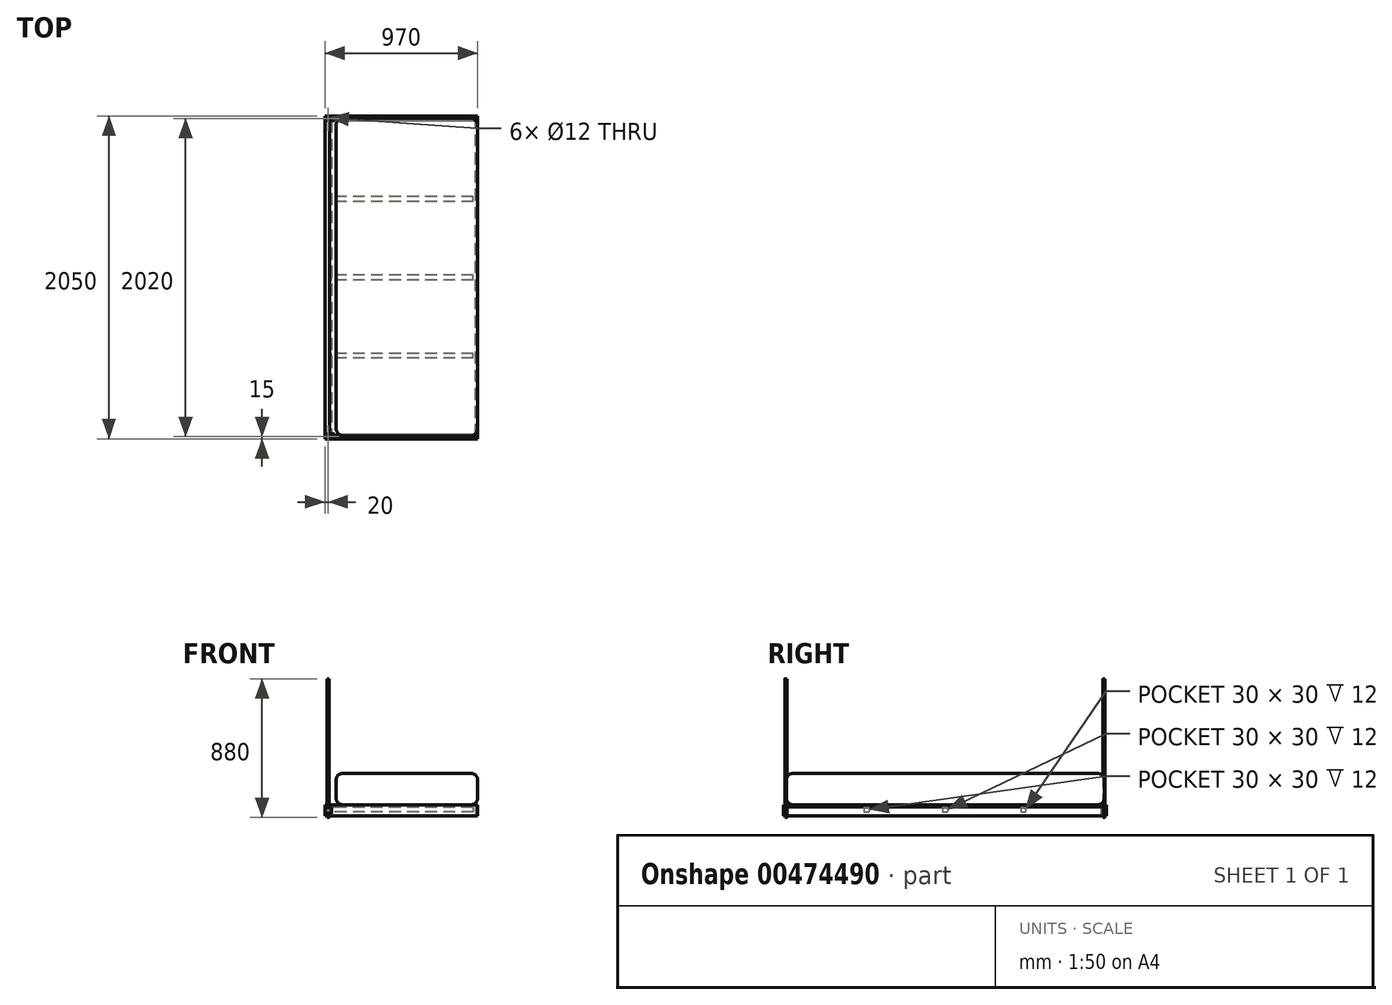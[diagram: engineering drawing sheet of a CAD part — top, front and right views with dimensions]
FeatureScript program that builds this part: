
annotation { "Feature Type Name" : "Feature", "Feature Type Description" : "" }
export const myFeature = defineFeature(function(context is Context, id is Id, definition is map)
    precondition{}
    {
        {
            var Q0;
            Q0=qCreatedBy(makeId("Top.planeOp"),FACE);
            var sketch = newSketch(context, id + "F0", { "sketchPlane" : qUnion([Q0])});
            skLineSegment(sketch, "E0.bottom", {"start": v(0, 0) * mm, "end": v(970, 0) * mm});
            skLineSegment(sketch, "E0.top", {"start": v(0, 2050) * mm, "end": v(970, 2050) * mm});
            skLineSegment(sketch, "E0.left", {"start": v(0, 0) * mm, "end": v(0, 2050) * mm});
            skLineSegment(sketch, "E0.right", {"start": v(970, 0) * mm, "end": v(970, 2050) * mm});
            skSolve(sketch);
        }
        {
            var Q0;
            Q0=qCreatedBy(makeId("Front.planeOp"),FACE);
            var sketch = newSketch(context, id + "F1", { "sketchPlane" : qUnion([Q0])});
            skLineSegment(sketch, "E1.bottom", {"start": v(0, 0) * mm, "end": v(42, 0) * mm});
            skLineSegment(sketch, "E1.top", {"start": v(0, 70) * mm, "end": v(30, 70) * mm});
            skLineSegment(sketch, "E1.left", {"start": v(0, 0) * mm, "end": v(0, 70) * mm});
            skLineSegment(sketch, "E1.right", {"start": v(30, 58.33) * mm, "end": v(30, 70) * mm});
            skLineSegment(sketch, "E2.bottom", {"start": v(30, 58.33) * mm, "end": v(42, 58.33) * mm});
            skLineSegment(sketch, "E2.right", {"start": v(42, 58.33) * mm, "end": v(42, 0) * mm});
            skSolve(sketch);
        }
        {
            var Q0;
            Q0 = qSketchRegion(id + "F1", true);
            var Q1;
            Q1=sQuery(id+"F0.wireOp",VERTEX,"E0.left.end");
            extrude(context, id + "F2", {"entities" : qUnion([Q0]), "endBound" : BoundingType.UP_TO_VERTEX, "oppositeDirection" : true, "endBoundEntityVertex" : qUnion([Q1]), "depth" : 25 * mm});
        }
        {
            var Q0;
            Q0=makeQuery(id+"F2.opExtrude","SWEPT_FACE",FACE,{"disambiguationData":[OSD([sQuery(id+"F1.wireOp",EDGE,"E1.left")])]});
            var sketch = newSketch(context, id + "F3", { "sketchPlane" : qUnion([Q0])});
            skLineSegment(sketch, "E3.bottom", {"start": v(0, 70) * mm, "end": v(-30, 70) * mm});
            skLineSegment(sketch, "E3.top", {"start": v(0, 55) * mm, "end": v(-30, 55) * mm});
            skLineSegment(sketch, "E3.left", {"start": v(0, 70) * mm, "end": v(0, 55) * mm});
            skLineSegment(sketch, "E3.right", {"start": v(-30, 70) * mm, "end": v(-30, 55) * mm});
            skLineSegment(sketch, "E4.bottom", {"start": v(0, 15) * mm, "end": v(-30, 15) * mm});
            skLineSegment(sketch, "E4.top", {"start": v(0, 0) * mm, "end": v(-30, 0) * mm});
            skLineSegment(sketch, "E4.left", {"start": v(0, 15) * mm, "end": v(0, 0) * mm});
            skLineSegment(sketch, "E4.right", {"start": v(-30, 15) * mm, "end": v(-30, 0) * mm});
            skLineSegment(sketch, "E5", {"start": v(-1025, 70) * mm, "end": v(-1025, 0) * mm, "construction": true});
            skLineSegment(sketch, "E6.MirrorCS", {"start": v(-2020, 70) * mm, "end": v(-2020, 55) * mm});
            skLineSegment(sketch, "E7.MirrorCS", {"start": v(-2050, 15) * mm, "end": v(-2020, 15) * mm});
            skLineSegment(sketch, "E8.MirrorCS", {"start": v(-2050, 0) * mm, "end": v(-2020, 0) * mm});
            skLineSegment(sketch, "E9.MirrorCS", {"start": v(-2020, 15) * mm, "end": v(-2020, 0) * mm});
            skLineSegment(sketch, "E10.MirrorCS", {"start": v(-2050, 55) * mm, "end": v(-2020, 55) * mm});
            skLineSegment(sketch, "E11.MirrorCS", {"start": v(-2050, 15) * mm, "end": v(-2050, 0) * mm});
            skLineSegment(sketch, "E12.MirrorCS", {"start": v(-2050, 70) * mm, "end": v(-2020, 70) * mm});
            skLineSegment(sketch, "E13.MirrorCS", {"start": v(-2050, 70) * mm, "end": v(-2050, 55) * mm});
            skSolve(sketch);
        }
        {
            var Q0;
            Q0 = qSketchRegion(id + "F3", true);
            extrude(context, id + "F4", {"entities" : qUnion([Q0]), "operationType" : NewBodyOperationType.REMOVE, "endBound" : BoundingType.THROUGH_ALL, "oppositeDirection" : true, "depth" : 25 * mm});
        }
        {
            var Q0;
            Q0=makeQuery(id+"F2.opExtrude","SWEPT_FACE",FACE,{"disambiguationData":[OSD([sQuery(id+"F1.wireOp",EDGE,"E2.right")])]});
            var sketch = newSketch(context, id + "F5", { "sketchPlane" : qUnion([Q0])});
            skLineSegment(sketch, "E14.bottom", {"start": v(512.5, 55) * mm, "end": v(542.5, 55) * mm});
            skLineSegment(sketch, "E14.top", {"start": v(512.5, 25) * mm, "end": v(542.5, 25) * mm});
            skLineSegment(sketch, "E14.left", {"start": v(512.5, 55) * mm, "end": v(512.5, 25) * mm});
            skLineSegment(sketch, "E14.right", {"start": v(542.5, 55) * mm, "end": v(542.5, 25) * mm});
            skLineSegment(sketch, "E15.1.0.0", {"start": v(1040, 55) * mm, "end": v(1040, 25) * mm});
            skLineSegment(sketch, "E15.1.0.1", {"start": v(1010, 55) * mm, "end": v(1010, 25) * mm});
            skLineSegment(sketch, "E15.1.0.2", {"start": v(1010, 25) * mm, "end": v(1040, 25) * mm});
            skLineSegment(sketch, "E15.1.0.3", {"start": v(1010, 55) * mm, "end": v(1040, 55) * mm});
            skLineSegment(sketch, "E15.2.0.0", {"start": v(1537.5, 55) * mm, "end": v(1537.5, 25) * mm});
            skLineSegment(sketch, "E15.2.0.1", {"start": v(1507.5, 55) * mm, "end": v(1507.5, 25) * mm});
            skLineSegment(sketch, "E15.2.0.2", {"start": v(1507.5, 25) * mm, "end": v(1537.5, 25) * mm});
            skLineSegment(sketch, "E15.2.0.3", {"start": v(1507.5, 55) * mm, "end": v(1537.5, 55) * mm});
            skLineSegment(sketch, "E15.direction1", {"start": v(512.5, 25) * mm, "end": v(1010, 25) * mm, "construction": true});
            skLineSegment(sketch, "E16", {"start": v(1025, 25) * mm, "end": v(1025, 0) * mm, "construction": true});
            skSolve(sketch);
        }
        {
            var Q0;
            Q0 = qSketchRegion(id + "F5", true);
            var Q1;
            Q1=makeQuery(id+"F2.opExtrude","SWEPT_FACE",FACE,{"disambiguationData":[OSD([sQuery(id+"F1.wireOp",EDGE,"E1.right")])]});
            extrude(context, id + "F6", {"entities" : qUnion([Q0]), "operationType" : NewBodyOperationType.REMOVE, "endBound" : BoundingType.UP_TO_SURFACE, "oppositeDirection" : true, "endBoundEntityFace" : qUnion([Q1]), "depth" : 25 * mm});
        }
        {
            var Q0;
            Q0 = qSketchRegion(id + "F5", true);
            var Q1;
            {var subQ0=sQuery(id+"F1.wireOp",EDGE,"E1.right");Q1=makeQuery(id+"F6.boolean.opBoolean","MERGE",FACE,{"derivedFrom":[makeQuery(id+"F2.opExtrude","SWEPT_FACE",FACE,{"disambiguationData":[OSD([subQ0])]}),makeQuery(id+"F6.opExtrude","CAP_FACE",FACE,{"disambiguationData":[OSD([subQ0]),ownerDisambiguation([makeQuery(id+"F5.imprint","IMPRINT",EDGE,{"derivedFrom":sQuery(id+"F5.wireOp",EDGE,"E14.bottom")})])],"isStart":false}),makeQuery(id+"F6.opExtrude","CAP_FACE",FACE,{"disambiguationData":[OSD([subQ0]),ownerDisambiguation([makeQuery(id+"F5.imprint","IMPRINT",EDGE,{"derivedFrom":sQuery(id+"F5.wireOp",EDGE,"E15.1.0.0")})])],"isStart":false}),makeQuery(id+"F6.opExtrude","CAP_FACE",FACE,{"disambiguationData":[OSD([subQ0]),ownerDisambiguation([makeQuery(id+"F5.imprint","IMPRINT",EDGE,{"derivedFrom":sQuery(id+"F5.wireOp",EDGE,"E15.2.0.0")})])],"isStart":false}),makeQuery(id+"F6.opExtrude","CAP_FACE",FACE,{"disambiguationData":[OSD([subQ0]),ownerDisambiguation([makeQuery(id+"F5.imprint","IMPRINT",EDGE,{"derivedFrom":sQuery(id+"F5.wireOp",EDGE,"E15.3.0.0")})])],"isStart":false})]});}
            extrude(context, id + "F7", {"entities" : qUnion([Q0]), "depth" : 900 * mm, "hasSecondDirection" : true, "secondDirectionBound" : SecondDirectionBoundingType.UP_TO_SURFACE, "secondDirectionOppositeDirection" : true, "secondDirectionBoundEntityFace" : qUnion([Q1]), "secondDirectionDepth" : 25 * mm});
        }
        {
            var Q0;
            {var subQ0=sQuery(id+"F1.wireOp",EDGE,"E1.bottom");var subQ1=sQuery(id+"F1.wireOp",EDGE,"E1.left");var subQ2=sQuery(id+"F1.wireOp",EDGE,"E2.right");Q0=makeQuery(id+"F4.boolean.opBoolean","SPLIT",FACE,{"disambiguationData":[TD([makeQuery(id+"F2.opExtrude","SWEPT_FACE",FACE,{"disambiguationData":[OSD([subQ0])]})])],"derivedFrom":makeQuery(id+"F2.opExtrude","CAP_FACE",FACE,{"disambiguationData":[OSD([subQ0,sQuery(id+"F1.wireOp",EDGE,"E1.top"),subQ1,sQuery(id+"F1.wireOp",EDGE,"E1.right"),sQuery(id+"F1.wireOp",EDGE,"E2.bottom"),subQ2])],"isStart":true})});}
            var sketch = newSketch(context, id + "F8", { "sketchPlane" : qUnion([Q0])});
            skLineSegment(sketch, "E17.0.0", {"start": v(42, 15) * mm, "end": v(0, 15) * mm});
            skLineSegment(sketch, "E18.1", {"start": v(0, 70) * mm, "end": v(0, 55) * mm});
            skLineSegment(sketch, "E19", {"start": v(0, 70) * mm, "end": v(970, 70) * mm});
            skLineSegment(sketch, "E20", {"start": v(970, 70) * mm, "end": v(970, 0) * mm});
            skLineSegment(sketch, "E21.1", {"start": v(42, 55) * mm, "end": v(42, 55) * mm});
            skPoint(sketch, "E21.3", {"position": v(42, 35) * mm});
            skLineSegment(sketch, "E22.0", {"start": v(42, 55) * mm, "end": v(42, 15) * mm});
            skLineSegment(sketch, "E22.1", {"start": v(42, 55) * mm, "end": v(0, 55) * mm});
            skLineSegment(sketch, "E23", {"start": v(42, 0) * mm, "end": v(970, 0) * mm});
            skLineSegment(sketch, "E24", {"start": v(0, 15) * mm, "end": v(0, 0) * mm});
            skLineSegment(sketch, "E25", {"start": v(0, 0) * mm, "end": v(42, 0) * mm});
            skSolve(sketch);
        }
        {
            var Q0;
            Q0 = qSketchRegion(id + "F8", true);
            var Q1;
            Q1=makeQuery(id+"F4.boolean.opBoolean","COPY",FACE,{"derivedFrom":makeQuery(id+"F4.opExtrude","SWEPT_FACE",FACE,{"disambiguationData":[OSD([sQuery(id+"F3.wireOp",EDGE,"E4.right")])]})});
            extrude(context, id + "F9", {"entities" : qUnion([Q0]), "endBound" : BoundingType.UP_TO_SURFACE, "oppositeDirection" : true, "endBoundEntityFace" : qUnion([Q1]), "depth" : 25 * mm});
        }
        {
            var Q0;
            Q0=sQuery(id+"F0.wireOp",EDGE,"E0.left");
            cPoint(context, id + "F10", {"entities" : qUnion([Q0]), "parameter" : 0.5});
        }
        {
            var Q0;
            Q0=qCreatedBy(makeId("Front.planeOp"),FACE);
            var Q1;
            Q1 = qCreatedBy(id + "F10" ,VERTEX);
            cPlane(context, id + "F11", {"entities" : qUnion([Q0, Q1]), "cplaneType" : CPlaneType.PLANE_POINT, "offset" : 25 * mm, "width" : 150 * mm, "height" : 150 * mm});
        }
        {
            var Q0;
            Q0=makeQuery(id+"F9.opExtrude","SWEPT_FACE",FACE,{"disambiguationData":[OSD([sQuery(id+"F8.wireOp",EDGE,"E19")])]});
            var sketch = newSketch(context, id + "F12", { "sketchPlane" : qUnion([Q0])});
            skLineSegment(sketch, "E26.bottom", {"start": v(60, 30) * mm, "end": v(970, 30) * mm});
            skLineSegment(sketch, "E26.top", {"start": v(60, 18) * mm, "end": v(970, 18) * mm});
            skLineSegment(sketch, "E26.left", {"start": v(60, 30) * mm, "end": v(60, 18) * mm});
            skLineSegment(sketch, "E26.right", {"start": v(970, 30) * mm, "end": v(970, 18) * mm});
            skSolve(sketch);
        }
        {
            var Q0;
            Q0 = qSketchRegion(id + "F12", true);
            var Q1;
            {var subQ3=sQuery(id+"F1.wireOp",EDGE,"E2.bottom");Q1=makeQuery(id+"F6.boolean.opBoolean","SPLIT",FACE,{"disambiguationData":[TD([makeQuery(id+"F4.boolean.opBoolean","COPY",FACE,{"derivedFrom":makeQuery(id+"F4.opExtrude","SWEPT_FACE",FACE,{"disambiguationData":[OSD([sQuery(id+"F3.wireOp",EDGE,"E3.right")])]})})])],"derivedFrom":makeQuery(id+"F4.boolean.opBoolean","MERGE",FACE,{"derivedFrom":[makeQuery(id+"F2.opExtrude","SWEPT_FACE",FACE,{"disambiguationData":[OSD([subQ3])]}),makeQuery(id+"F4.opExtrude","SWEPT_FACE",FACE,{"disambiguationData":[OSD([sQuery(id+"F3.wireOp",EDGE,"E3.top")])]}),makeQuery(id+"F4.opExtrude","SWEPT_FACE",FACE,{"disambiguationData":[OSD([sQuery(id+"F3.wireOp",EDGE,"E10.MirrorCS")])]})]})});}
            extrude(context, id + "F13", {"entities" : qUnion([Q0]), "operationType" : NewBodyOperationType.REMOVE, "endBound" : BoundingType.UP_TO_SURFACE, "oppositeDirection" : true, "endBoundEntityFace" : qUnion([Q1]), "depth" : 25 * mm});
        }
        {
            var Q0;
            Q0=makeQuery(id+"F9.opExtrude","SWEPT_BODY",BODY,{"disambiguationData":[OSD([sQuery(id+"F8.wireOp",EDGE,"E17.0.0"),sQuery(id+"F8.wireOp",EDGE,"E17.0.1"),sQuery(id+"F8.wireOp",EDGE,"E17.0.2"),sQuery(id+"F8.wireOp",EDGE,"E17.1.0"),sQuery(id+"F8.wireOp",EDGE,"E17.1.1"),sQuery(id+"F8.wireOp",EDGE,"E17.1.2"),sQuery(id+"F8.wireOp",EDGE,"E18.0"),sQuery(id+"F8.wireOp",EDGE,"E18.1"),sQuery(id+"F8.wireOp",EDGE,"E19"),sQuery(id+"F8.wireOp",EDGE,"E20"),sQuery(id+"F8.wireOp",EDGE,"2vJveZOf-mYqw-0ZfC-QnWn-0q5ONevqvfo5"),sQuery(id+"F8.wireOp",EDGE,"E21.0"),sQuery(id+"F8.wireOp",EDGE,"E21.1"),sQuery(id+"F8.wireOp",EDGE,"E21.2")])]});
            var Q1;
            Q1=qCreatedBy(id+"F11.planeOp",FACE);
            mirror(context, id + "F14", {"entities" : qUnion([Q0]), "mirrorPlane" : qUnion([Q1])});
        }
        {
            var Q0;
            Q0=makeQuery(id+"F2.opExtrude","SWEPT_FACE",FACE,{"disambiguationData":[OSD([sQuery(id+"F1.wireOp",EDGE,"E1.top")])]});
            var sketch = newSketch(context, id + "F15", { "sketchPlane" : qUnion([Q0])});
            skCircle(sketch, "E27.MirrorC", {"center": v(20, 15) * mm, "radius": 6 * mm});
            skLineSegment(sketch, "E28", {"start": v(20, 2035) * mm, "end": v(0, 2035) * mm, "construction": true});
            skLineSegment(sketch, "E29", {"start": v(20, 15) * mm, "end": v(0, 15) * mm, "construction": true});
            skCircle(sketch, "E30", {"center": v(20, 2035) * mm, "radius": 6 * mm});
            skSolve(sketch);
        }
        {
            var Q0;
            Q0 = qSketchRegion(id + "F15", true);
            extrude(context, id + "F16", {"entities" : qUnion([Q0]), "operationType" : NewBodyOperationType.REMOVE, "endBound" : BoundingType.THROUGH_ALL, "oppositeDirection" : true, "depth" : 25 * mm});
        }
        {
            var Q0;
            Q0=makeQuery(id+"F14.opPattern","COPY",FACE,{"derivedFrom":makeQuery(id+"F13.boolean.opBoolean","COPY",FACE,{"derivedFrom":makeQuery(id+"F13.opExtrude","SWEPT_FACE",FACE,{"disambiguationData":[OSD([sQuery(id+"F12.wireOp",EDGE,"E26.top")])]})}),"instanceName":"1"});
            var sketch = newSketch(context, id + "F17", { "sketchPlane" : qUnion([Q0])});
            skLineSegment(sketch, "E31.bottom", {"start": v(970, 58.33) * mm, "end": v(958, 58.33) * mm});
            skLineSegment(sketch, "E31.top", {"start": v(970, 0) * mm, "end": v(958, 0) * mm});
            skLineSegment(sketch, "E31.left", {"start": v(970, 58.33) * mm, "end": v(970, 0) * mm});
            skLineSegment(sketch, "E31.right", {"start": v(958, 58.33) * mm, "end": v(958, 0) * mm});
            skSolve(sketch);
        }
        {
            var Q0;
            Q0 = qSketchRegion(id + "F17", true);
            var Q1;
            Q1=makeQuery(id+"F13.boolean.opBoolean","COPY",FACE,{"derivedFrom":makeQuery(id+"F13.opExtrude","SWEPT_FACE",FACE,{"disambiguationData":[OSD([sQuery(id+"F12.wireOp",EDGE,"E26.top")])]})});
            extrude(context, id + "F18", {"entities" : qUnion([Q0]), "operationType" : NewBodyOperationType.REMOVE, "endBound" : BoundingType.UP_TO_SURFACE, "endBoundEntityFace" : qUnion([Q1]), "depth" : 25 * mm});
        }
        {
            var Q0;
            Q0 = qSketchRegion(id + "F17", true);
            var Q1;
            {var subQ0=sQuery(id+"F12.wireOp",EDGE,"E26.top");Q1=makeQuery(id+"F18.boolean.opBoolean","MERGE",FACE,{"derivedFrom":[makeQuery(id+"F13.boolean.opBoolean","COPY",FACE,{"derivedFrom":makeQuery(id+"F13.opExtrude","SWEPT_FACE",FACE,{"disambiguationData":[OSD([subQ0])]})}),makeQuery(id+"F18.opExtrude","CAP_FACE",FACE,{"disambiguationData":[OSD([subQ0])],"isStart":false})]});}
            extrude(context, id + "F19", {"entities" : qUnion([Q0]), "endBound" : BoundingType.UP_TO_SURFACE, "endBoundEntityFace" : qUnion([Q1]), "depth" : 25 * mm});
        }
        {
            var Q0;
            Q0=makeQuery(id+"F6.boolean.opBoolean","SPLIT",FACE,{"disambiguationData":[TD([makeQuery(id+"F2.opExtrude","CAP_FACE",FACE,{"disambiguationData":[OSD([dummyQuery(id+"F2.vertexPlane.planeOp",FACE)])],"isStart":false})])],"derivedFrom":makeQuery(id+"F4.boolean.opBoolean","MERGE",FACE,{"derivedFrom":[makeQuery(id+"F2.opExtrude","SWEPT_FACE",FACE,{"disambiguationData":[OSD([sQuery(id+"F1.wireOp",EDGE,"E2.bottom")])]}),makeQuery(id+"F4.opExtrude","SWEPT_FACE",FACE,{"disambiguationData":[OSD([sQuery(id+"F3.wireOp",EDGE,"E3.top")])]}),makeQuery(id+"F4.opExtrude","SWEPT_FACE",FACE,{"disambiguationData":[OSD([sQuery(id+"F3.wireOp",EDGE,"E10.MirrorCS")])]})]})});
            var sketch = newSketch(context, id + "F20", { "sketchPlane" : qUnion([Q0])});
            skLineSegment(sketch, "E32.0", {"start": v(60, 2032) * mm, "end": v(970, 2032) * mm});
            skLineSegment(sketch, "E32.1", {"start": v(60, 2020) * mm, "end": v(60, 2032) * mm});
            skLineSegment(sketch, "E32.2", {"start": v(30, 2020) * mm, "end": v(60, 2020) * mm});
            skLineSegment(sketch, "E32.3", {"start": v(30, 2020) * mm, "end": v(30, 30) * mm});
            skLineSegment(sketch, "E32.4", {"start": v(970, 18) * mm, "end": v(970, 2032) * mm});
            skLineSegment(sketch, "E32.5", {"start": v(30, 30) * mm, "end": v(60, 30) * mm});
            skLineSegment(sketch, "E32.6", {"start": v(60, 30) * mm, "end": v(60, 18) * mm});
            skLineSegment(sketch, "E32.7", {"start": v(60, 18) * mm, "end": v(970, 18) * mm});
            skPoint(sketch, "E33.orphan", {"position": v(0, 2020) * mm});
            skPoint(sketch, "E34.orphan", {"position": v(0, 30) * mm});
            skSolve(sketch);
        }
        {
            var Q0;
            Q0 = qSketchRegion(id + "F20", true);
            extrude(context, id + "F21", {"entities" : qUnion([Q0]), "depth" : 12 * mm});
        }
        {
            var Q0;
            Q0 = qSketchRegion(id + "F15", true);
            extrude(context, id + "F22", {"entities" : qUnion([Q0]), "depth" : 800 * mm, "hasSecondDirection" : true, "secondDirectionOppositeDirection" : true, "secondDirectionDepth" : 80 * mm});
        }
        {
            var Q0;
            Q0=makeQuery(id+"F21.opExtrude","CAP_FACE",FACE,{"disambiguationData":[OSD([sQuery(id+"F20.wireOp",EDGE,"E32.0"),sQuery(id+"F20.wireOp",EDGE,"E32.1"),sQuery(id+"F20.wireOp",EDGE,"E32.2"),sQuery(id+"F20.wireOp",EDGE,"E32.3"),sQuery(id+"F20.wireOp",EDGE,"E32.4"),sQuery(id+"F20.wireOp",EDGE,"E32.5"),sQuery(id+"F20.wireOp",EDGE,"E32.6"),sQuery(id+"F20.wireOp",EDGE,"E32.7")])],"isStart":false});
            var sketch = newSketch(context, id + "F23", { "sketchPlane" : qUnion([Q0])});
            skLineSegment(sketch, "E35.bottom", {"start": v(120, 2038) * mm, "end": v(920, 2038) * mm});
            skLineSegment(sketch, "E35.top", {"start": v(120, 18) * mm, "end": v(920, 18) * mm});
            skLineSegment(sketch, "E35.left", {"start": v(70, 1988) * mm, "end": v(70, 68) * mm});
            skLineSegment(sketch, "E35.right", {"start": v(970, 1988) * mm, "end": v(970, 68) * mm});
            skPoint(sketch, "E36.visualSharp", {"position": v(70, 2038) * mm});
            skArc(sketch, "E36.filletArc", {"start": v(120, 2038) * mm, "mid": v(84.64, 2023.36) * mm, "end": v(70, 1988) * mm});
            skPoint(sketch, "E37.visualSharp", {"position": v(970, 2038) * mm});
            skArc(sketch, "E37.filletArc", {"start": v(970, 1988) * mm, "mid": v(955.36, 2023.36) * mm, "end": v(920, 2038) * mm});
            skPoint(sketch, "E38.visualSharp", {"position": v(970, 18) * mm});
            skArc(sketch, "E38.filletArc", {"start": v(920, 18) * mm, "mid": v(955.36, 32.64) * mm, "end": v(970, 68) * mm});
            skPoint(sketch, "E39.visualSharp", {"position": v(70, 18) * mm});
            skArc(sketch, "E39.filletArc", {"start": v(70, 68) * mm, "mid": v(84.64, 32.64) * mm, "end": v(120, 18) * mm});
            skSolve(sketch);
        }
        {
            var Q0;
            Q0 = qSketchRegion(id + "F23", true);
            extrude(context, id + "F24", {"entities" : qUnion([Q0]), "depth" : 200 * mm});
        }
        {
            var Q0;
            Q0=makeQuery(id+"F24.opExtrude","CAP_FACE",FACE,{"disambiguationData":[OSD([sQuery(id+"F23.wireOp",EDGE,"E35.bottom"),sQuery(id+"F23.wireOp",EDGE,"E35.top"),sQuery(id+"F23.wireOp",EDGE,"E35.left"),sQuery(id+"F23.wireOp",EDGE,"E35.right"),sQuery(id+"F23.wireOp",EDGE,"E36.filletArc"),sQuery(id+"F23.wireOp",EDGE,"E37.filletArc"),sQuery(id+"F23.wireOp",EDGE,"E38.filletArc"),sQuery(id+"F23.wireOp",EDGE,"E39.filletArc")])],"isStart":false});
            var Q1;
            Q1=makeQuery(id+"F24.opExtrude","CAP_FACE",FACE,{"disambiguationData":[OSD([sQuery(id+"F23.wireOp",EDGE,"E35.bottom"),sQuery(id+"F23.wireOp",EDGE,"E35.top"),sQuery(id+"F23.wireOp",EDGE,"E35.left"),sQuery(id+"F23.wireOp",EDGE,"E35.right"),sQuery(id+"F23.wireOp",EDGE,"E36.filletArc"),sQuery(id+"F23.wireOp",EDGE,"E37.filletArc"),sQuery(id+"F23.wireOp",EDGE,"E38.filletArc"),sQuery(id+"F23.wireOp",EDGE,"E39.filletArc")])],"isStart":true});
            fillet(context, id + "F25", {"entities" : qUnion([Q0, Q1]), "radius" : 50 * mm, "tangentPropagation" : true, "rho" : 0.5, "crossSection" : FilletCrossSection.CONIC, "allowEdgeOverflow" : false});
        }
    });
